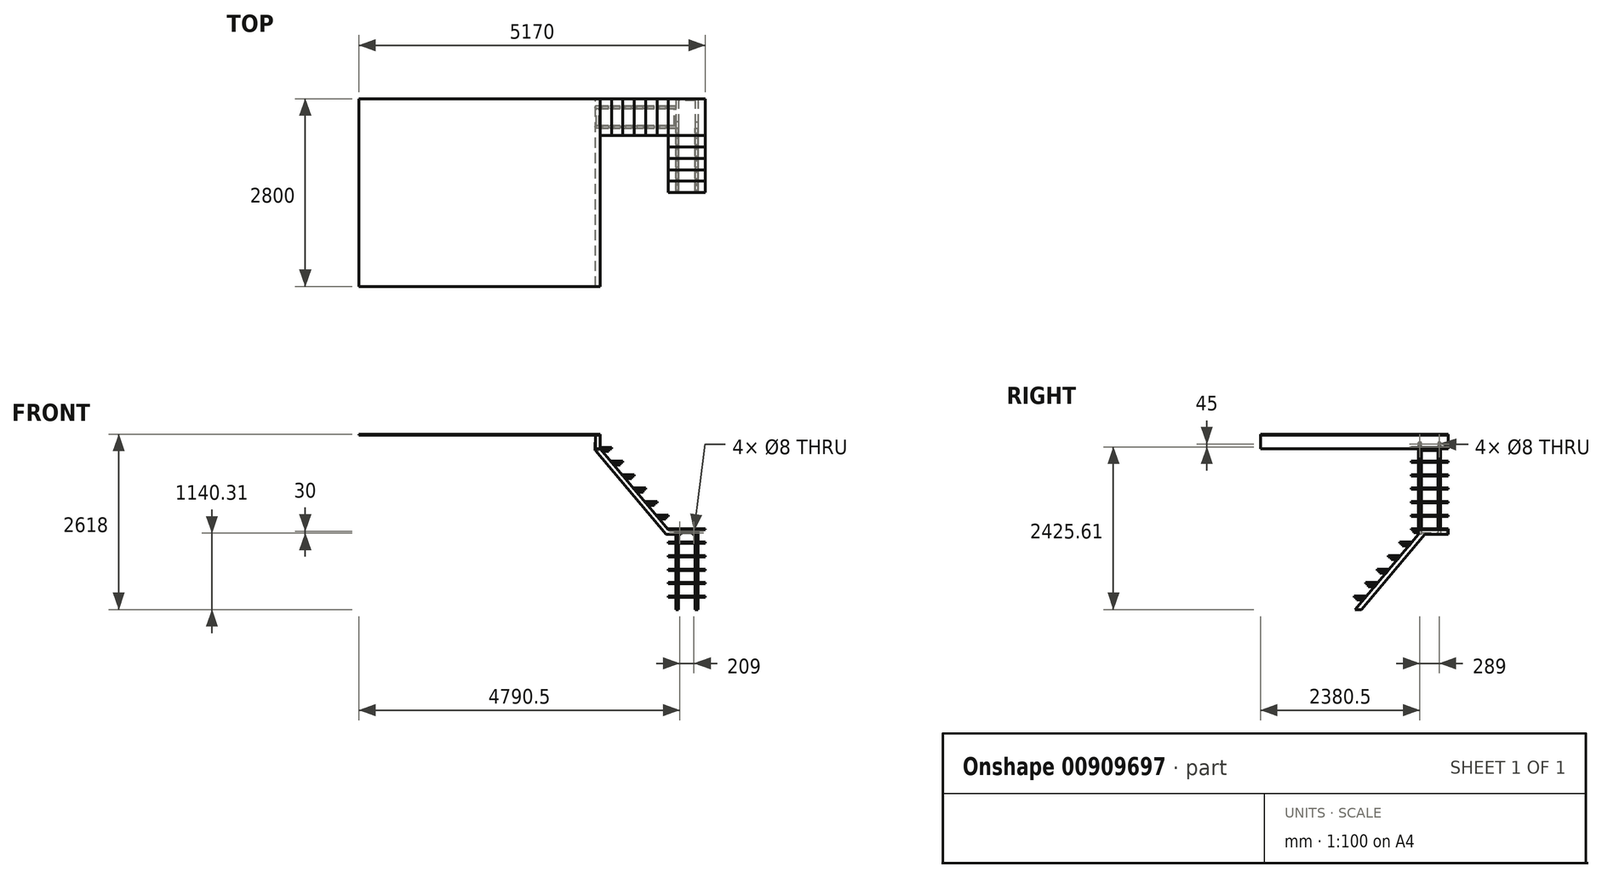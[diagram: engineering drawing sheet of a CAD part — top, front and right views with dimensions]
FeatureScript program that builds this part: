
annotation { "Feature Type Name" : "Feature", "Feature Type Description" : "" }
export const myFeature = defineFeature(function(context is Context, id is Id, definition is map)
    precondition{}
    {
        {
            var Q0;
            Q0=qCreatedBy(makeId("Front.planeOp"),FACE);
            var sketch = newSketch(context, id + "F0", { "sketchPlane" : qUnion([Q0])});
            skLineSegment(sketch, "E0", {"start": v(0, 0) * mm, "end": v(0, 2618) * mm, "construction": true});
            skLineSegment(sketch, "E1", {"start": v(0, 0) * mm, "end": v(1570, 0) * mm, "construction": true});
            skLineSegment(sketch, "E2", {"start": v(0, 2618) * mm, "end": v(-785.9, 2618) * mm, "construction": true});
            skLineSegment(sketch, "E3", {"start": v(0, 2400) * mm, "end": v(-71, 2400) * mm, "construction": true});
            skLineSegment(sketch, "E4", {"start": v(0, 2600) * mm, "end": v(-785.9, 2600) * mm, "construction": true});
            skLineSegment(sketch, "E5", {"start": v(-71, 2400) * mm, "end": v(-71, 2600) * mm, "construction": true});
            skLineSegment(sketch, "E6", {"start": v(0, 2416.62) * mm, "end": v(170, 2416.62) * mm, "construction": true});
            skLineSegment(sketch, "E7", {"start": v(170, 2416.62) * mm, "end": v(170, 2215.23) * mm, "construction": true});
            skLineSegment(sketch, "E8", {"start": v(170, 2215.23) * mm, "end": v(340, 2215.23) * mm, "construction": true});
            skLineSegment(sketch, "E9", {"start": v(340, 2215.23) * mm, "end": v(340, 2013.85) * mm, "construction": true});
            skLineSegment(sketch, "E10", {"start": v(340, 2013.85) * mm, "end": v(510, 2013.85) * mm, "construction": true});
            skLineSegment(sketch, "E11", {"start": v(510, 2013.85) * mm, "end": v(510, 1812.46) * mm, "construction": true});
            skLineSegment(sketch, "E12", {"start": v(510, 1812.46) * mm, "end": v(680, 1812.46) * mm, "construction": true});
            skLineSegment(sketch, "E13", {"start": v(680, 1812.46) * mm, "end": v(680, 1611.08) * mm, "construction": true});
            skLineSegment(sketch, "E14", {"start": v(680, 1611.08) * mm, "end": v(850, 1611.08) * mm, "construction": true});
            skLineSegment(sketch, "E15", {"start": v(850, 1611.08) * mm, "end": v(850, 1409.7) * mm, "construction": true});
            skLineSegment(sketch, "E16", {"start": v(850, 1409.7) * mm, "end": v(1020, 1409.7) * mm, "construction": true});
            skLineSegment(sketch, "E17", {"start": v(1020, 1409.7) * mm, "end": v(1020, 1208.3) * mm, "construction": true});
            skLineSegment(sketch, "E18", {"start": v(0, 2416.62) * mm, "end": v(0, 2618) * mm, "construction": true});
            skLineSegment(sketch, "E19", {"start": v(1570, 0) * mm, "end": v(1570, 1208.3) * mm, "construction": true});
            skLineSegment(sketch, "E20", {"start": v(1020, 1208.3) * mm, "end": v(1570, 1208.3) * mm, "construction": true});
            skLineSegment(sketch, "E21", {"start": v(1570, 1190.3) * mm, "end": v(1020, 1190.3) * mm, "construction": true});
            skLineSegment(sketch, "E22", {"start": v(1020, 1208.3) * mm, "end": v(1020, 1190.3) * mm, "construction": true});
            skSolve(sketch);
        }
        {
            var Q0;
            Q0=qCreatedBy(makeId("Front.planeOp"),FACE);
            cPlane(context, id + "F1", {"entities" : qUnion([Q0]), "cplaneType" : CPlaneType.OFFSET, "offset" : 110.5 * mm, "width" : 150 * mm, "height" : 150 * mm});
        }
        {
            var Q0;
            Q0=qCreatedBy(id+"F1.planeOp",FACE);
            var sketch = newSketch(context, id + "F2", { "sketchPlane" : qUnion([Q0])});
            skLineSegment(sketch, "E23", {"start": v(0, 2400) * mm, "end": v(1020, 1190.3) * mm});
            skLineSegment(sketch, "E24", {"start": v(1020, 1190.3) * mm, "end": v(1130.5, 1190.3) * mm});
            skLineSegment(sketch, "E25", {"start": v(1130.5, 1190.3) * mm, "end": v(1130.5, 1120.3) * mm});
            skLineSegment(sketch, "E26", {"start": v(1130.5, 1120.3) * mm, "end": v(987.46, 1120.3) * mm});
            skLineSegment(sketch, "E27", {"start": v(987.46, 1120.3) * mm, "end": v(-71, 2375.61) * mm});
            skLineSegment(sketch, "E28", {"start": v(1020, 1190.3) * mm, "end": v(987.46, 1120.3) * mm, "construction": true});
            skLineSegment(sketch, "E29", {"start": v(0, 2400) * mm, "end": v(-71, 2400) * mm});
            skLineSegment(sketch, "E30", {"start": v(-71, 2400) * mm, "end": v(-71, 2375.61) * mm});
            skSolve(sketch);
        }
        {
            var Q0;
            Q0=qCreatedBy(makeId("Front.planeOp"),FACE);
            var sketch = newSketch(context, id + "F3", { "sketchPlane" : qUnion([Q0])});
            skLineSegment(sketch, "E31.bottom", {"start": v(-71, 2600) * mm, "end": v(0, 2600) * mm});
            skLineSegment(sketch, "E31.top", {"start": v(-71, 2400) * mm, "end": v(0, 2400) * mm});
            skLineSegment(sketch, "E31.left", {"start": v(-71, 2600) * mm, "end": v(-71, 2400) * mm});
            skLineSegment(sketch, "E31.right", {"start": v(0, 2600) * mm, "end": v(0, 2400) * mm});
            skSolve(sketch);
        }
        {
            var Q0;
            Q0 = qSketchRegion(id + "F3", true);
            extrude(context, id + "F4", {"entities" : qUnion([Q0]), "depth" : 2800 * mm, "offsetDistance" : 25 * mm});
        }
        {
            var Q0;
            Q0=qCreatedBy(makeId("Front.planeOp"),FACE);
            var sketch = newSketch(context, id + "F5", { "sketchPlane" : qUnion([Q0])});
            skLineSegment(sketch, "E32.bottom", {"start": v(1020, 1208.3) * mm, "end": v(1570, 1208.3) * mm});
            skLineSegment(sketch, "E32.top", {"start": v(1020, 1190.3) * mm, "end": v(1570, 1190.3) * mm});
            skLineSegment(sketch, "E32.left", {"start": v(1020, 1208.3) * mm, "end": v(1020, 1190.3) * mm});
            skLineSegment(sketch, "E32.right", {"start": v(1570, 1208.3) * mm, "end": v(1570, 1190.3) * mm});
            skSolve(sketch);
        }
        {
            var Q0;
            Q0=qCreatedBy(makeId("Front.planeOp"),FACE);
            var sketch = newSketch(context, id + "F6", { "sketchPlane" : qUnion([Q0])});
            skLineSegment(sketch, "E33.bottom", {"start": v(0, 2600) * mm, "end": v(-3600, 2600) * mm});
            skLineSegment(sketch, "E33.top", {"start": v(0, 2618) * mm, "end": v(-3600, 2618) * mm});
            skLineSegment(sketch, "E33.left", {"start": v(0, 2600) * mm, "end": v(0, 2618) * mm});
            skLineSegment(sketch, "E33.right", {"start": v(-3600, 2600) * mm, "end": v(-3600, 2618) * mm});
            skSolve(sketch);
        }
        {
            var Q0;
            Q0 = qSketchRegion(id + "F6", true);
            extrude(context, id + "F7", {"entities" : qUnion([Q0]), "depth" : 2800 * mm, "offsetDistance" : 25 * mm});
        }
        {
            var Q0;
            Q0 = qSketchRegion(id + "F5", true);
            extrude(context, id + "F8", {"entities" : qUnion([Q0]), "depth" : 550 * mm, "offsetDistance" : 25 * mm});
        }
        {
            var Q0;
            Q0 = qSketchRegion(id + "F2", true);
            extrude(context, id + "F9", {"entities" : qUnion([Q0]), "depth" : 40 * mm, "offsetDistance" : 25 * mm});
        }
        {
            var Q0;
            Q0=makeQuery(id+"F9.opExtrude","SWEPT_FACE",FACE,{"disambiguationData":[OSD([sQuery(id+"F2.wireOp",EDGE,"E25")])]});
            cPlane(context, id + "F10", {"entities" : qUnion([Q0]), "cplaneType" : CPlaneType.OFFSET, "offset" : 0 * mm, "width" : 150 * mm, "height" : 150 * mm});
        }
        {
            var Q0;
            Q0=qCreatedBy(makeId("Front.planeOp"),FACE);
            var sketch = newSketch(context, id + "F11", { "sketchPlane" : qUnion([Q0])});
            skLineSegment(sketch, "E34.bottom", {"start": v(0, 2416.62) * mm, "end": v(170, 2416.62) * mm});
            skLineSegment(sketch, "E34.top", {"start": v(0, 2398.62) * mm, "end": v(170, 2398.62) * mm});
            skLineSegment(sketch, "E34.left", {"start": v(0, 2416.62) * mm, "end": v(0, 2398.62) * mm});
            skLineSegment(sketch, "E34.right", {"start": v(170, 2416.62) * mm, "end": v(170, 2398.62) * mm});
            skLineSegment(sketch, "E35.bottom", {"start": v(170, 2215.23) * mm, "end": v(340, 2215.23) * mm});
            skLineSegment(sketch, "E35.top", {"start": v(170, 2197.23) * mm, "end": v(340, 2197.23) * mm});
            skLineSegment(sketch, "E35.left", {"start": v(170, 2215.23) * mm, "end": v(170, 2197.23) * mm});
            skLineSegment(sketch, "E35.right", {"start": v(340, 2215.23) * mm, "end": v(340, 2197.23) * mm});
            skLineSegment(sketch, "E36.bottom", {"start": v(340, 2013.85) * mm, "end": v(510, 2013.85) * mm});
            skLineSegment(sketch, "E36.left", {"start": v(340, 2013.85) * mm, "end": v(340, 1995.85) * mm});
            skLineSegment(sketch, "E37.bottom", {"start": v(510, 1812.46) * mm, "end": v(680, 1812.46) * mm});
            skLineSegment(sketch, "E37.top", {"start": v(510, 1794.46) * mm, "end": v(680, 1794.46) * mm});
            skLineSegment(sketch, "E37.left", {"start": v(510, 1812.46) * mm, "end": v(510, 1794.46) * mm});
            skLineSegment(sketch, "E37.right", {"start": v(680, 1812.46) * mm, "end": v(680, 1794.46) * mm});
            skLineSegment(sketch, "E38.bottom", {"start": v(680, 1593.08) * mm, "end": v(850, 1593.08) * mm});
            skLineSegment(sketch, "E38.top", {"start": v(680, 1611.08) * mm, "end": v(850, 1611.08) * mm});
            skLineSegment(sketch, "E38.left", {"start": v(680, 1593.08) * mm, "end": v(680, 1611.08) * mm});
            skLineSegment(sketch, "E38.right", {"start": v(850, 1593.08) * mm, "end": v(850, 1611.08) * mm});
            skLineSegment(sketch, "E39.bottom", {"start": v(850, 1409.7) * mm, "end": v(1020, 1409.7) * mm});
            skLineSegment(sketch, "E39.top", {"start": v(850, 1391.7) * mm, "end": v(1020, 1391.7) * mm});
            skLineSegment(sketch, "E39.left", {"start": v(850, 1409.7) * mm, "end": v(850, 1391.7) * mm});
            skLineSegment(sketch, "E39.right", {"start": v(1020, 1409.7) * mm, "end": v(1020, 1391.7) * mm});
            skLineSegment(sketch, "E40", {"start": v(510, 2013.85) * mm, "end": v(510, 1995.85) * mm});
            skLineSegment(sketch, "E41", {"start": v(510, 1995.85) * mm, "end": v(340, 1995.85) * mm});
            skSolve(sketch);
        }
        {
            var Q0;
            Q0 = qSketchRegion(id + "F11", true);
            extrude(context, id + "F12", {"entities" : qUnion([Q0]), "depth" : 550 * mm, "offsetDistance" : 25 * mm});
        }
        {
            var Q0;
            Q0=qCreatedBy(id+"F10.planeOp",FACE);
            var sketch = newSketch(context, id + "F13", { "sketchPlane" : qUnion([Q0])});
            skLineSegment(sketch, "E42", {"start": v(-550, 1208.3) * mm, "end": v(-550, 1006.92) * mm, "construction": true});
            skLineSegment(sketch, "E43", {"start": v(-550, 1006.92) * mm, "end": v(-720, 1006.92) * mm, "construction": true});
            skLineSegment(sketch, "E44", {"start": v(-720, 1006.92) * mm, "end": v(-720, 805.54) * mm, "construction": true});
            skLineSegment(sketch, "E45", {"start": v(-720, 805.54) * mm, "end": v(-890, 805.54) * mm, "construction": true});
            skLineSegment(sketch, "E46", {"start": v(-890, 805.54) * mm, "end": v(-890, 604.15) * mm, "construction": true});
            skLineSegment(sketch, "E47", {"start": v(-890, 604.15) * mm, "end": v(-1060, 604.15) * mm, "construction": true});
            skLineSegment(sketch, "E48", {"start": v(-1060, 604.15) * mm, "end": v(-1060, 402.77) * mm, "construction": true});
            skLineSegment(sketch, "E49", {"start": v(-1060, 402.77) * mm, "end": v(-1230, 402.77) * mm, "construction": true});
            skLineSegment(sketch, "E50", {"start": v(-1230, 402.77) * mm, "end": v(-1230, 201.38) * mm, "construction": true});
            skLineSegment(sketch, "E51", {"start": v(-1230, 201.38) * mm, "end": v(-1400, 201.38) * mm, "construction": true});
            skLineSegment(sketch, "E52", {"start": v(-1400, 201.38) * mm, "end": v(-1400, 0) * mm, "construction": true});
            skLineSegment(sketch, "E53", {"start": v(-1400, 0) * mm, "end": v(0, 0) * mm, "construction": true});
            skSolve(sketch);
        }
        {
            var Q0;
            Q0=makeQuery(id+"F8.opExtrude","SWEPT_FACE",FACE,{"disambiguationData":[OSD([sQuery(id+"F5.wireOp",EDGE,"E32.right")])]});
            var sketch = newSketch(context, id + "F14", { "sketchPlane" : qUnion([Q0])});
            skLineSegment(sketch, "E54.bottom", {"start": v(-720, 1006.92) * mm, "end": v(-550, 1006.92) * mm});
            skLineSegment(sketch, "E54.top", {"start": v(-720, 988.92) * mm, "end": v(-550, 988.92) * mm});
            skLineSegment(sketch, "E54.left", {"start": v(-720, 1006.92) * mm, "end": v(-720, 988.92) * mm});
            skLineSegment(sketch, "E54.right", {"start": v(-550, 1006.92) * mm, "end": v(-550, 988.92) * mm});
            skLineSegment(sketch, "E55.bottom", {"start": v(-890, 805.54) * mm, "end": v(-720, 805.54) * mm});
            skLineSegment(sketch, "E55.top", {"start": v(-890, 787.54) * mm, "end": v(-720, 787.54) * mm});
            skLineSegment(sketch, "E55.left", {"start": v(-890, 805.54) * mm, "end": v(-890, 787.54) * mm});
            skLineSegment(sketch, "E55.right", {"start": v(-720, 805.54) * mm, "end": v(-720, 787.54) * mm});
            skLineSegment(sketch, "E56.bottom", {"start": v(-1060, 604.15) * mm, "end": v(-890, 604.15) * mm});
            skLineSegment(sketch, "E56.top", {"start": v(-1060, 586.15) * mm, "end": v(-890, 586.15) * mm});
            skLineSegment(sketch, "E56.left", {"start": v(-1060, 604.15) * mm, "end": v(-1060, 586.15) * mm});
            skLineSegment(sketch, "E56.right", {"start": v(-890, 604.15) * mm, "end": v(-890, 586.15) * mm});
            skLineSegment(sketch, "E57.bottom", {"start": v(-1230, 402.77) * mm, "end": v(-1060, 402.77) * mm});
            skLineSegment(sketch, "E57.top", {"start": v(-1230, 384.77) * mm, "end": v(-1060, 384.77) * mm});
            skLineSegment(sketch, "E57.left", {"start": v(-1230, 402.77) * mm, "end": v(-1230, 384.77) * mm});
            skLineSegment(sketch, "E57.right", {"start": v(-1060, 402.77) * mm, "end": v(-1060, 384.77) * mm});
            skLineSegment(sketch, "E58.bottom", {"start": v(-1400, 201.38) * mm, "end": v(-1230, 201.38) * mm});
            skLineSegment(sketch, "E58.top", {"start": v(-1400, 183.38) * mm, "end": v(-1230, 183.38) * mm});
            skLineSegment(sketch, "E58.left", {"start": v(-1400, 201.38) * mm, "end": v(-1400, 183.38) * mm});
            skLineSegment(sketch, "E58.right", {"start": v(-1230, 201.38) * mm, "end": v(-1230, 183.38) * mm});
            skSolve(sketch);
        }
        {
            var Q0;
            Q0 = qSketchRegion(id + "F14", true);
            extrude(context, id + "F15", {"entities" : qUnion([Q0]), "oppositeDirection" : true, "depth" : 550 * mm, "offsetDistance" : 25 * mm});
        }
        {
            var Q0;
            Q0=qCreatedBy(id+"F10.planeOp",FACE);
            var sketch = newSketch(context, id + "F16", { "sketchPlane" : qUnion([Q0])});
            skLineSegment(sketch, "E59", {"start": v(0, 1190.3) * mm, "end": v(-439.5, 1190.3) * mm});
            skLineSegment(sketch, "E60", {"start": v(-439.1, 1120.3) * mm, "end": v(-1384.8, 0) * mm});
            skLineSegment(sketch, "E61", {"start": v(0, 1120.3) * mm, "end": v(-347.48, 1120.3) * mm});
            skLineSegment(sketch, "E62", {"start": v(-347.48, 1120.3) * mm, "end": v(-1293.2, 0) * mm});
            skLineSegment(sketch, "E63", {"start": v(-1384.8, 0) * mm, "end": v(-1293.2, 0) * mm});
            skLineSegment(sketch, "E64", {"start": v(0, 1190.3) * mm, "end": v(0, 1120.3) * mm});
            skLineSegment(sketch, "E65", {"start": v(-439.5, 1190.3) * mm, "end": v(-439.5, 1120.3) * mm});
            skLineSegment(sketch, "E66", {"start": v(-439.5, 1120.3) * mm, "end": v(-439.1, 1120.3) * mm});
            skLineSegment(sketch, "E67", {"start": v(-439.1, 1120.3) * mm, "end": v(-347.48, 1120.3) * mm, "construction": true});
            skSolve(sketch);
        }
        {
            var Q0;
            Q0=makeQuery(id+"F16.imprint","IMPRINT",FACE,{"disambiguationData":[TD([[makeQuery(id+"F16.imprint","IMPRINT",EDGE,{"derivedFrom":sQuery(id+"F16.wireOp",EDGE,"E59")}),1.0]])]});
            extrude(context, id + "F17", {"entities" : qUnion([Q0]), "depth" : 40 * mm, "offsetDistance" : 25 * mm});
        }
        {
            var Q0;
            Q0=qCreatedBy(id+"F1.planeOp",FACE);
            var sketch = newSketch(context, id + "F18", { "sketchPlane" : qUnion([Q0])});
            skLineSegment(sketch, "E68", {"start": v(0, 2400) * mm, "end": v(130, 2400) * mm});
            skLineSegment(sketch, "E69", {"start": v(130, 2400) * mm, "end": v(130, 2360) * mm});
            skLineSegment(sketch, "E70", {"start": v(130, 2360) * mm, "end": v(33.73, 2360) * mm});
            skLineSegment(sketch, "E71", {"start": v(33.73, 2360) * mm, "end": v(0, 2400) * mm});
            skLineSegment(sketch, "E72", {"start": v(170, 2197.23) * mm, "end": v(300.97, 2197.23) * mm});
            skLineSegment(sketch, "E73", {"start": v(300.97, 2197.23) * mm, "end": v(300.97, 2157.23) * mm});
            skLineSegment(sketch, "E74", {"start": v(300.97, 2157.23) * mm, "end": v(204.7, 2157.23) * mm});
            skLineSegment(sketch, "E75", {"start": v(204.7, 2157.23) * mm, "end": v(170, 2197.23) * mm});
            skLineSegment(sketch, "E76", {"start": v(340, 1995.85) * mm, "end": v(470.78, 1995.85) * mm});
            skLineSegment(sketch, "E77", {"start": v(470.78, 1995.85) * mm, "end": v(470.78, 1955.85) * mm});
            skLineSegment(sketch, "E78", {"start": v(470.78, 1955.85) * mm, "end": v(374.5, 1955.85) * mm});
            skLineSegment(sketch, "E79", {"start": v(374.5, 1955.85) * mm, "end": v(340, 1995.85) * mm});
            skLineSegment(sketch, "E80", {"start": v(510, 1794.46) * mm, "end": v(640.58, 1794.46) * mm});
            skLineSegment(sketch, "E81", {"start": v(640.58, 1794.46) * mm, "end": v(640.58, 1754.46) * mm});
            skLineSegment(sketch, "E82", {"start": v(640.58, 1754.46) * mm, "end": v(544.31, 1754.46) * mm});
            skLineSegment(sketch, "E83", {"start": v(544.31, 1754.46) * mm, "end": v(510, 1794.46) * mm});
            skLineSegment(sketch, "E84", {"start": v(680, 1593.08) * mm, "end": v(810.39, 1593.08) * mm});
            skLineSegment(sketch, "E85", {"start": v(810.39, 1593.08) * mm, "end": v(810.39, 1553.08) * mm});
            skLineSegment(sketch, "E86", {"start": v(810.39, 1553.08) * mm, "end": v(714.12, 1553.08) * mm});
            skLineSegment(sketch, "E87", {"start": v(714.12, 1553.08) * mm, "end": v(680, 1593.08) * mm});
            skLineSegment(sketch, "E88", {"start": v(850, 1391.7) * mm, "end": v(980.2, 1391.7) * mm});
            skLineSegment(sketch, "E89", {"start": v(980.2, 1391.7) * mm, "end": v(980.2, 1351.7) * mm});
            skLineSegment(sketch, "E90", {"start": v(980.2, 1351.7) * mm, "end": v(883.92, 1351.7) * mm});
            skLineSegment(sketch, "E91", {"start": v(883.92, 1351.7) * mm, "end": v(850, 1391.7) * mm});
            skSolve(sketch);
        }
        {
            var Q0;
            Q0 = qSketchRegion(id + "F18", true);
            extrude(context, id + "F19", {"entities" : qUnion([Q0]), "depth" : 40 * mm, "offsetDistance" : 25 * mm});
        }
        {
            var Q0;
            Q0=makeQuery(id+"F12.opExtrude","CAP_FACE",FACE,{"disambiguationData":[OSD([sQuery(id+"F11.wireOp",EDGE,"E34.bottom"),sQuery(id+"F11.wireOp",EDGE,"E34.top"),sQuery(id+"F11.wireOp",EDGE,"E34.left"),sQuery(id+"F11.wireOp",EDGE,"E34.right")])],"isStart":false});
            cPlane(context, id + "F20", {"entities" : qUnion([Q0]), "cplaneType" : CPlaneType.OFFSET, "offset" : 110.5 * mm, "oppositeDirection" : true, "width" : 150 * mm, "height" : 150 * mm});
        }
        {
            var Q0;
            Q0=qCreatedBy(id+"F20.planeOp",FACE);
            var sketch = newSketch(context, id + "F21", { "sketchPlane" : qUnion([Q0])});
            skLineSegment(sketch, "E92", {"start": v(0, 2400) * mm, "end": v(1020, 1190.3) * mm});
            skLineSegment(sketch, "E93", {"start": v(1020, 1190.3) * mm, "end": v(1130.5, 1190.3) * mm});
            skLineSegment(sketch, "E94", {"start": v(1130.5, 1190.3) * mm, "end": v(1130.5, 1120.3) * mm});
            skLineSegment(sketch, "E95", {"start": v(1130.5, 1120.3) * mm, "end": v(987.46, 1120.3) * mm});
            skLineSegment(sketch, "E96", {"start": v(987.46, 1120.3) * mm, "end": v(-71, 2375.61) * mm});
            skLineSegment(sketch, "E97", {"start": v(1020, 1190.3) * mm, "end": v(987.46, 1120.3) * mm, "construction": true});
            skLineSegment(sketch, "E98", {"start": v(0, 2400) * mm, "end": v(-71, 2400) * mm});
            skLineSegment(sketch, "E99", {"start": v(-71, 2400) * mm, "end": v(-71, 2375.61) * mm});
            skSolve(sketch);
        }
        {
            var Q0;
            Q0=makeQuery(id+"F21.imprint","IMPRINT",FACE,{"disambiguationData":[TD([[makeQuery(id+"F21.imprint","IMPRINT",EDGE,{"derivedFrom":sQuery(id+"F21.wireOp",EDGE,"E92")}),-1.0]])]});
            extrude(context, id + "F22", {"entities" : qUnion([Q0]), "oppositeDirection" : true, "depth" : 40 * mm, "offsetDistance" : 25 * mm});
        }
        {
            var Q0;
            Q0=makeQuery(id+"F9.opExtrude","SWEPT_FACE",FACE,{"disambiguationData":[OSD([sQuery(id+"F2.wireOp",EDGE,"E30")])]});
            var sketch = newSketch(context, id + "F23", { "sketchPlane" : qUnion([Q0])});
            skLineSegment(sketch, "E100.bottom", {"start": v(110.5, 2375.61) * mm, "end": v(150.5, 2375.61) * mm});
            skLineSegment(sketch, "E100.top", {"start": v(110.5, 2495.61) * mm, "end": v(150.5, 2495.61) * mm});
            skLineSegment(sketch, "E100.left", {"start": v(110.5, 2375.61) * mm, "end": v(110.5, 2495.61) * mm});
            skLineSegment(sketch, "E100.right", {"start": v(150.5, 2375.61) * mm, "end": v(150.5, 2495.61) * mm});
            skCircle(sketch, "E101", {"center": v(130.5, 2470.61) * mm, "radius": 4 * mm});
            skCircle(sketch, "E102", {"center": v(130.5, 2425.61) * mm, "radius": 4 * mm});
            skLineSegment(sketch, "E103", {"start": v(130.5, 2470.61) * mm, "end": v(130.5, 2425.61) * mm, "construction": true});
            skLineSegment(sketch, "E104", {"start": v(130.5, 2470.61) * mm, "end": v(130.5, 2495.61) * mm, "construction": true});
            skLineSegment(sketch, "E105.bottom", {"start": v(399.5, 2375.61) * mm, "end": v(439.5, 2375.61) * mm});
            skLineSegment(sketch, "E105.top", {"start": v(399.5, 2495.61) * mm, "end": v(439.5, 2495.61) * mm});
            skLineSegment(sketch, "E105.left", {"start": v(399.5, 2375.61) * mm, "end": v(399.5, 2495.61) * mm});
            skLineSegment(sketch, "E105.right", {"start": v(439.5, 2375.61) * mm, "end": v(439.5, 2495.61) * mm});
            skCircle(sketch, "E106", {"center": v(419.5, 2470.61) * mm, "radius": 4 * mm});
            skCircle(sketch, "E107", {"center": v(419.5, 2425.61) * mm, "radius": 4 * mm});
            skLineSegment(sketch, "E108", {"start": v(419.5, 2470.61) * mm, "end": v(419.5, 2425.61) * mm, "construction": true});
            skLineSegment(sketch, "E109", {"start": v(419.5, 2470.61) * mm, "end": v(419.5, 2495.61) * mm, "construction": true});
            skSolve(sketch);
        }
        {
            var Q0;
            Q0 = qSketchRegion(id + "F23", true);
            extrude(context, id + "F24", {"entities" : qUnion([Q0]), "depth" : 3 * mm, "offsetDistance" : 25 * mm});
        }
        {
            var Q0;
            Q0=makeQuery(id+"F8.opExtrude","SWEPT_FACE",FACE,{"disambiguationData":[OSD([sQuery(id+"F5.wireOp",EDGE,"E32.right")])]});
            cPlane(context, id + "F25", {"entities" : qUnion([Q0]), "cplaneType" : CPlaneType.OFFSET, "offset" : 110.5 * mm, "oppositeDirection" : true, "width" : 150 * mm, "height" : 150 * mm});
        }
        {
            var Q0;
            Q0=qCreatedBy(id+"F25.planeOp",FACE);
            var sketch = newSketch(context, id + "F26", { "sketchPlane" : qUnion([Q0])});
            skLineSegment(sketch, "E110", {"start": v(0, 1190.3) * mm, "end": v(-439.5, 1190.3) * mm});
            skLineSegment(sketch, "E111", {"start": v(-439.1, 1120.3) * mm, "end": v(-1384.8, 0) * mm});
            skLineSegment(sketch, "E112", {"start": v(0, 1120.3) * mm, "end": v(-347.48, 1120.3) * mm});
            skLineSegment(sketch, "E113", {"start": v(-347.48, 1120.3) * mm, "end": v(-1293.2, 0) * mm});
            skLineSegment(sketch, "E114", {"start": v(-1384.8, 0) * mm, "end": v(-1293.2, 0) * mm});
            skLineSegment(sketch, "E115", {"start": v(0, 1190.3) * mm, "end": v(0, 1120.3) * mm});
            skLineSegment(sketch, "E116", {"start": v(-439.5, 1190.3) * mm, "end": v(-439.5, 1120.3) * mm});
            skLineSegment(sketch, "E117", {"start": v(-439.5, 1120.3) * mm, "end": v(-439.1, 1120.3) * mm});
            skLineSegment(sketch, "E118", {"start": v(-439.1, 1120.3) * mm, "end": v(-347.48, 1120.3) * mm, "construction": true});
            skSolve(sketch);
        }
        {
            var Q0;
            Q0=makeQuery(id+"F26.imprint","IMPRINT",FACE,{"disambiguationData":[TD([[makeQuery(id+"F26.imprint","IMPRINT",EDGE,{"derivedFrom":sQuery(id+"F26.wireOp",EDGE,"E110")}),1.0]])]});
            extrude(context, id + "F27", {"entities" : qUnion([Q0]), "oppositeDirection" : true, "depth" : 40 * mm, "offsetDistance" : 25 * mm});
        }
        {
            var Q0;
            Q0=makeQuery(id+"F22.opExtrude","CAP_FACE",FACE,{"disambiguationData":[OSD([sQuery(id+"F21.wireOp",EDGE,"E92"),sQuery(id+"F21.wireOp",EDGE,"E93"),sQuery(id+"F21.wireOp",EDGE,"E94"),sQuery(id+"F21.wireOp",EDGE,"E95"),sQuery(id+"F21.wireOp",EDGE,"E96"),sQuery(id+"F21.wireOp",EDGE,"E98"),sQuery(id+"F21.wireOp",EDGE,"E99")])],"isStart":true});
            var sketch = newSketch(context, id + "F28", { "sketchPlane" : qUnion([Q0])});
            skLineSegment(sketch, "E119", {"start": v(0, 2400) * mm, "end": v(130, 2400) * mm});
            skLineSegment(sketch, "E120", {"start": v(130, 2400) * mm, "end": v(130, 2360) * mm});
            skLineSegment(sketch, "E121", {"start": v(130, 2360) * mm, "end": v(33.73, 2360) * mm});
            skLineSegment(sketch, "E122", {"start": v(33.73, 2360) * mm, "end": v(0, 2400) * mm});
            skLineSegment(sketch, "E123", {"start": v(170.97, 2197.23) * mm, "end": v(300.97, 2197.23) * mm});
            skLineSegment(sketch, "E124", {"start": v(300.97, 2197.23) * mm, "end": v(300.97, 2157.23) * mm});
            skLineSegment(sketch, "E125", {"start": v(300.97, 2157.23) * mm, "end": v(204.7, 2157.23) * mm});
            skLineSegment(sketch, "E126", {"start": v(204.7, 2157.23) * mm, "end": v(170.97, 2197.23) * mm});
            skLineSegment(sketch, "E127", {"start": v(340.78, 1995.85) * mm, "end": v(470.78, 1995.85) * mm});
            skLineSegment(sketch, "E128", {"start": v(470.78, 1995.85) * mm, "end": v(470.78, 1955.85) * mm});
            skLineSegment(sketch, "E129", {"start": v(470.78, 1955.85) * mm, "end": v(374.5, 1955.85) * mm});
            skLineSegment(sketch, "E130", {"start": v(374.5, 1955.85) * mm, "end": v(340.78, 1995.85) * mm});
            skLineSegment(sketch, "E131", {"start": v(510.58, 1794.46) * mm, "end": v(640.58, 1794.46) * mm});
            skLineSegment(sketch, "E132", {"start": v(640.58, 1794.46) * mm, "end": v(640.58, 1754.46) * mm});
            skLineSegment(sketch, "E133", {"start": v(640.58, 1754.46) * mm, "end": v(544.31, 1754.46) * mm});
            skLineSegment(sketch, "E134", {"start": v(544.31, 1754.46) * mm, "end": v(510.58, 1794.46) * mm});
            skLineSegment(sketch, "E135", {"start": v(680.39, 1593.08) * mm, "end": v(810.39, 1593.08) * mm});
            skLineSegment(sketch, "E136", {"start": v(810.39, 1593.08) * mm, "end": v(810.39, 1553.08) * mm});
            skLineSegment(sketch, "E137", {"start": v(810.39, 1553.08) * mm, "end": v(714.12, 1553.08) * mm});
            skLineSegment(sketch, "E138", {"start": v(714.12, 1553.08) * mm, "end": v(680.39, 1593.08) * mm});
            skLineSegment(sketch, "E139", {"start": v(850.2, 1391.7) * mm, "end": v(980.2, 1391.7) * mm});
            skLineSegment(sketch, "E140", {"start": v(980.2, 1391.7) * mm, "end": v(980.2, 1351.7) * mm});
            skLineSegment(sketch, "E141", {"start": v(980.2, 1351.7) * mm, "end": v(883.92, 1351.7) * mm});
            skLineSegment(sketch, "E142", {"start": v(883.92, 1351.7) * mm, "end": v(850.2, 1391.7) * mm});
            skSolve(sketch);
        }
        {
            var Q0;
            Q0 = qSketchRegion(id + "F28", true);
            extrude(context, id + "F29", {"entities" : qUnion([Q0]), "oppositeDirection" : true, "depth" : 40 * mm, "offsetDistance" : 25 * mm});
        }
        {
            var Q0;
            Q0=makeQuery(id+"F17.opExtrude","CAP_FACE",FACE,{"disambiguationData":[OSD([sQuery(id+"F16.wireOp",EDGE,"E59"),sQuery(id+"F16.wireOp",EDGE,"E60"),sQuery(id+"F16.wireOp",EDGE,"E61"),sQuery(id+"F16.wireOp",EDGE,"E62"),sQuery(id+"F16.wireOp",EDGE,"E63"),sQuery(id+"F16.wireOp",EDGE,"E64"),sQuery(id+"F16.wireOp",EDGE,"E65")])],"isStart":false});
            var sketch = newSketch(context, id + "F30", { "sketchPlane" : qUnion([Q0])});
            skLineSegment(sketch, "E143", {"start": v(-680, 988.92) * mm, "end": v(-550, 988.92) * mm});
            skLineSegment(sketch, "E144", {"start": v(-550, 988.92) * mm, "end": v(-583.77, 948.92) * mm});
            skLineSegment(sketch, "E145", {"start": v(-583.77, 948.92) * mm, "end": v(-680, 948.92) * mm});
            skLineSegment(sketch, "E146", {"start": v(-680, 948.92) * mm, "end": v(-680, 988.92) * mm});
            skLineSegment(sketch, "E147.bottom", {"start": v(-510, 1190.3) * mm, "end": v(-439.5, 1190.3) * mm});
            skLineSegment(sketch, "E147.top", {"start": v(-510, 1150.3) * mm, "end": v(-439.5, 1150.3) * mm});
            skLineSegment(sketch, "E147.left", {"start": v(-510, 1190.3) * mm, "end": v(-510, 1150.3) * mm});
            skLineSegment(sketch, "E147.right", {"start": v(-439.5, 1190.3) * mm, "end": v(-439.5, 1150.3) * mm});
            skLineSegment(sketch, "E148", {"start": v(-850, 787.54) * mm, "end": v(-720, 787.54) * mm});
            skLineSegment(sketch, "E149", {"start": v(-720, 787.54) * mm, "end": v(-753.77, 747.54) * mm});
            skLineSegment(sketch, "E150", {"start": v(-753.77, 747.54) * mm, "end": v(-850, 747.54) * mm});
            skLineSegment(sketch, "E151", {"start": v(-850, 747.54) * mm, "end": v(-850, 787.54) * mm});
            skLineSegment(sketch, "E152", {"start": v(-1190, 384.77) * mm, "end": v(-1060, 384.77) * mm});
            skLineSegment(sketch, "E153", {"start": v(-1060, 384.77) * mm, "end": v(-1093.77, 344.77) * mm});
            skLineSegment(sketch, "E154", {"start": v(-1093.77, 344.77) * mm, "end": v(-1190, 344.77) * mm});
            skLineSegment(sketch, "E155", {"start": v(-1190, 344.77) * mm, "end": v(-1190, 384.77) * mm});
            skLineSegment(sketch, "E156", {"start": v(-1020, 586.15) * mm, "end": v(-890, 586.15) * mm});
            skLineSegment(sketch, "E157", {"start": v(-890, 586.15) * mm, "end": v(-923.77, 546.15) * mm});
            skLineSegment(sketch, "E158", {"start": v(-923.77, 546.15) * mm, "end": v(-1020, 546.15) * mm});
            skLineSegment(sketch, "E159", {"start": v(-1020, 546.15) * mm, "end": v(-1020, 586.15) * mm});
            skLineSegment(sketch, "E160", {"start": v(-1360, 183.38) * mm, "end": v(-1230, 183.38) * mm});
            skLineSegment(sketch, "E161", {"start": v(-1230, 183.38) * mm, "end": v(-1263.77, 143.38) * mm});
            skLineSegment(sketch, "E162", {"start": v(-1263.77, 143.38) * mm, "end": v(-1360, 143.38) * mm});
            skLineSegment(sketch, "E163", {"start": v(-1360, 143.38) * mm, "end": v(-1360, 183.38) * mm});
            skSolve(sketch);
        }
        {
            var Q0;
            Q0 = qSketchRegion(id + "F30", true);
            extrude(context, id + "F31", {"entities" : qUnion([Q0]), "oppositeDirection" : true, "depth" : 40 * mm, "offsetDistance" : 25 * mm});
        }
        {
            var Q0;
            Q0=makeQuery(id+"F17.opExtrude","SWEPT_FACE",FACE,{"disambiguationData":[OSD([sQuery(id+"F16.wireOp",EDGE,"E64")])]});
            var sketch = newSketch(context, id + "F32", { "sketchPlane" : qUnion([Q0])});
            skLineSegment(sketch, "E164.bottom", {"start": v(-1210.5, 1190.3) * mm, "end": v(-1170.5, 1190.3) * mm});
            skLineSegment(sketch, "E164.top", {"start": v(-1210.5, 1120.3) * mm, "end": v(-1170.5, 1120.3) * mm});
            skLineSegment(sketch, "E164.left", {"start": v(-1210.5, 1190.3) * mm, "end": v(-1210.5, 1120.3) * mm});
            skLineSegment(sketch, "E164.right", {"start": v(-1170.5, 1190.3) * mm, "end": v(-1170.5, 1120.3) * mm});
            skLineSegment(sketch, "E165.bottom", {"start": v(-1419.5, 1190.3) * mm, "end": v(-1379.5, 1190.3) * mm});
            skLineSegment(sketch, "E165.top", {"start": v(-1419.5, 1120.3) * mm, "end": v(-1379.5, 1120.3) * mm});
            skLineSegment(sketch, "E165.left", {"start": v(-1419.5, 1190.3) * mm, "end": v(-1419.5, 1120.3) * mm});
            skLineSegment(sketch, "E165.right", {"start": v(-1379.5, 1190.3) * mm, "end": v(-1379.5, 1120.3) * mm});
            skCircle(sketch, "E166", {"center": v(-1399.5, 1170.3) * mm, "radius": 4 * mm});
            skCircle(sketch, "E167", {"center": v(-1399.5, 1140.3) * mm, "radius": 4 * mm});
            skCircle(sketch, "E168", {"center": v(-1190.5, 1170.3) * mm, "radius": 4 * mm});
            skCircle(sketch, "E169", {"center": v(-1190.5, 1140.3) * mm, "radius": 4 * mm});
            skLineSegment(sketch, "E170", {"start": v(-1399.5, 1190.3) * mm, "end": v(-1399.5, 1170.3) * mm, "construction": true});
            skLineSegment(sketch, "E171", {"start": v(-1399.5, 1140.3) * mm, "end": v(-1399.5, 1170.3) * mm, "construction": true});
            skLineSegment(sketch, "E172", {"start": v(-1190.5, 1140.3) * mm, "end": v(-1190.5, 1170.3) * mm, "construction": true});
            skLineSegment(sketch, "E173", {"start": v(-1190.5, 1190.3) * mm, "end": v(-1190.5, 1170.3) * mm, "construction": true});
            skSolve(sketch);
        }
        {
            var Q0;
            Q0 = qSketchRegion(id + "F32", true);
            extrude(context, id + "F33", {"entities" : qUnion([Q0]), "oppositeDirection" : true, "depth" : 3 * mm, "offsetDistance" : 25 * mm});
        }
        {
            var Q0;
            Q0=makeQuery(id+"F27.opExtrude","CAP_FACE",FACE,{"disambiguationData":[OSD([sQuery(id+"F26.wireOp",EDGE,"E110"),sQuery(id+"F26.wireOp",EDGE,"E111"),sQuery(id+"F26.wireOp",EDGE,"E112"),sQuery(id+"F26.wireOp",EDGE,"E113"),sQuery(id+"F26.wireOp",EDGE,"E114"),sQuery(id+"F26.wireOp",EDGE,"E115"),sQuery(id+"F26.wireOp",EDGE,"E116")])],"isStart":true});
            var sketch = newSketch(context, id + "F34", { "sketchPlane" : qUnion([Q0])});
            skLineSegment(sketch, "E174", {"start": v(-680, 988.92) * mm, "end": v(-550, 988.92) * mm});
            skLineSegment(sketch, "E175", {"start": v(-550, 988.92) * mm, "end": v(-583.77, 948.92) * mm});
            skLineSegment(sketch, "E176", {"start": v(-583.77, 948.92) * mm, "end": v(-680, 948.92) * mm});
            skLineSegment(sketch, "E177", {"start": v(-680, 948.92) * mm, "end": v(-680, 988.92) * mm});
            skLineSegment(sketch, "E178.bottom", {"start": v(-510, 1190.3) * mm, "end": v(-439.5, 1190.3) * mm});
            skLineSegment(sketch, "E178.top", {"start": v(-510, 1150.3) * mm, "end": v(-439.5, 1150.3) * mm});
            skLineSegment(sketch, "E178.left", {"start": v(-510, 1190.3) * mm, "end": v(-510, 1150.3) * mm});
            skLineSegment(sketch, "E178.right", {"start": v(-439.5, 1190.3) * mm, "end": v(-439.5, 1150.3) * mm});
            skLineSegment(sketch, "E179", {"start": v(-850, 787.54) * mm, "end": v(-720, 787.54) * mm});
            skLineSegment(sketch, "E180", {"start": v(-720, 787.54) * mm, "end": v(-753.77, 747.54) * mm});
            skLineSegment(sketch, "E181", {"start": v(-753.77, 747.54) * mm, "end": v(-850, 747.54) * mm});
            skLineSegment(sketch, "E182", {"start": v(-850, 747.54) * mm, "end": v(-850, 787.54) * mm});
            skLineSegment(sketch, "E183", {"start": v(-1190, 384.77) * mm, "end": v(-1060, 384.77) * mm});
            skLineSegment(sketch, "E184", {"start": v(-1060, 384.77) * mm, "end": v(-1093.77, 344.77) * mm});
            skLineSegment(sketch, "E185", {"start": v(-1093.77, 344.77) * mm, "end": v(-1190, 344.77) * mm});
            skLineSegment(sketch, "E186", {"start": v(-1190, 344.77) * mm, "end": v(-1190, 384.77) * mm});
            skLineSegment(sketch, "E187", {"start": v(-1020, 586.15) * mm, "end": v(-890, 586.15) * mm});
            skLineSegment(sketch, "E188", {"start": v(-890, 586.15) * mm, "end": v(-923.77, 546.15) * mm});
            skLineSegment(sketch, "E189", {"start": v(-923.77, 546.15) * mm, "end": v(-1020, 546.15) * mm});
            skLineSegment(sketch, "E190", {"start": v(-1020, 546.15) * mm, "end": v(-1020, 586.15) * mm});
            skLineSegment(sketch, "E191", {"start": v(-1360, 183.38) * mm, "end": v(-1230, 183.38) * mm});
            skLineSegment(sketch, "E192", {"start": v(-1230, 183.38) * mm, "end": v(-1263.77, 143.38) * mm});
            skLineSegment(sketch, "E193", {"start": v(-1263.77, 143.38) * mm, "end": v(-1360, 143.38) * mm});
            skLineSegment(sketch, "E194", {"start": v(-1360, 143.38) * mm, "end": v(-1360, 183.38) * mm});
            skSolve(sketch);
        }
        {
            var Q0;
            Q0 = qSketchRegion(id + "F34", true);
            extrude(context, id + "F35", {"entities" : qUnion([Q0]), "oppositeDirection" : true, "depth" : 40 * mm, "offsetDistance" : 25 * mm});
        }
        {
            var Q0;
            Q0=makeQuery(id+"F9.opExtrude","CAP_FACE",FACE,{"disambiguationData":[OSD([sQuery(id+"F2.wireOp",EDGE,"E23"),sQuery(id+"F2.wireOp",EDGE,"E24"),sQuery(id+"F2.wireOp",EDGE,"E25"),sQuery(id+"F2.wireOp",EDGE,"E26"),sQuery(id+"F2.wireOp",EDGE,"E27"),sQuery(id+"F2.wireOp",EDGE,"E29"),sQuery(id+"F2.wireOp",EDGE,"E30")])],"isStart":false});
            var sketch = newSketch(context, id + "F36", { "sketchPlane" : qUnion([Q0])});
            skLineSegment(sketch, "E195.bottom", {"start": v(-55.5, 2400) * mm, "end": v(-15.5, 2400) * mm});
            skLineSegment(sketch, "E195.top", {"start": v(-55.5, 2375) * mm, "end": v(-15.5, 2375) * mm});
            skLineSegment(sketch, "E195.left", {"start": v(-55.5, 2400) * mm, "end": v(-55.5, 2375) * mm});
            skLineSegment(sketch, "E195.right", {"start": v(-15.5, 2400) * mm, "end": v(-15.5, 2375) * mm});
            skPoint(sketch, "E196", {"position": v(-35.5, 2400) * mm});
            skSolve(sketch);
        }
        {
            var Q0;
            Q0 = qSketchRegion(id + "F36", true);
            extrude(context, id + "F37", {"entities" : qUnion([Q0]), "endBound" : BoundingType.UP_TO_NEXT, "depth" : 25 * mm, "offsetDistance" : 25 * mm});
        }
        {
            var Q0;
            Q0=makeQuery(id+"F17.opExtrude","CAP_FACE",FACE,{"disambiguationData":[OSD([sQuery(id+"F16.wireOp",EDGE,"E59"),sQuery(id+"F16.wireOp",EDGE,"E60"),sQuery(id+"F16.wireOp",EDGE,"E61"),sQuery(id+"F16.wireOp",EDGE,"E62"),sQuery(id+"F16.wireOp",EDGE,"E63"),sQuery(id+"F16.wireOp",EDGE,"E64"),sQuery(id+"F16.wireOp",EDGE,"E65")])],"isStart":false});
            var sketch = newSketch(context, id + "F38", { "sketchPlane" : qUnion([Q0])});
            skLineSegment(sketch, "E197.bottom", {"start": v(-25, 1190.3) * mm, "end": v(0, 1190.3) * mm});
            skLineSegment(sketch, "E197.top", {"start": v(-25, 1150.3) * mm, "end": v(0, 1150.3) * mm});
            skLineSegment(sketch, "E197.left", {"start": v(-25, 1190.3) * mm, "end": v(-25, 1150.3) * mm});
            skLineSegment(sketch, "E197.right", {"start": v(0, 1190.3) * mm, "end": v(0, 1150.3) * mm});
            skSolve(sketch);
        }
        {
            var Q0;
            Q0 = qSketchRegion(id + "F38", true);
            var Q1;
            Q1=makeQuery(id+"F27.opExtrude","CAP_FACE",FACE,{"disambiguationData":[OSD([sQuery(id+"F26.wireOp",EDGE,"E110"),sQuery(id+"F26.wireOp",EDGE,"E111"),sQuery(id+"F26.wireOp",EDGE,"E112"),sQuery(id+"F26.wireOp",EDGE,"E113"),sQuery(id+"F26.wireOp",EDGE,"E114"),sQuery(id+"F26.wireOp",EDGE,"E115"),sQuery(id+"F26.wireOp",EDGE,"E116")])],"isStart":false});
            extrude(context, id + "F39", {"entities" : qUnion([Q0]), "endBound" : BoundingType.UP_TO_SURFACE, "depth" : 25 * mm, "endBoundEntityFace" : qUnion([Q1]), "offsetDistance" : 25 * mm});
        }
        {
            var Q0;
            Q0=makeQuery(id+"F9.opExtrude","CAP_FACE",FACE,{"disambiguationData":[OSD([sQuery(id+"F2.wireOp",EDGE,"E23"),sQuery(id+"F2.wireOp",EDGE,"E24"),sQuery(id+"F2.wireOp",EDGE,"E25"),sQuery(id+"F2.wireOp",EDGE,"E26"),sQuery(id+"F2.wireOp",EDGE,"E27"),sQuery(id+"F2.wireOp",EDGE,"E29"),sQuery(id+"F2.wireOp",EDGE,"E30")])],"isStart":false});
            var sketch = newSketch(context, id + "F40", { "sketchPlane" : qUnion([Q0])});
            skLineSegment(sketch, "E198.bottom", {"start": v(1130.5, 1190.3) * mm, "end": v(1105.5, 1190.3) * mm});
            skLineSegment(sketch, "E198.top", {"start": v(1130.5, 1150.3) * mm, "end": v(1105.5, 1150.3) * mm});
            skLineSegment(sketch, "E198.left", {"start": v(1130.5, 1190.3) * mm, "end": v(1130.5, 1150.3) * mm});
            skLineSegment(sketch, "E198.right", {"start": v(1105.5, 1190.3) * mm, "end": v(1105.5, 1150.3) * mm});
            skSolve(sketch);
        }
        {
            var Q0;
            Q0 = qSketchRegion(id + "F40", true);
            extrude(context, id + "F41", {"entities" : qUnion([Q0]), "endBound" : BoundingType.UP_TO_NEXT, "depth" : 25 * mm, "offsetDistance" : 25 * mm});
        }
    });
